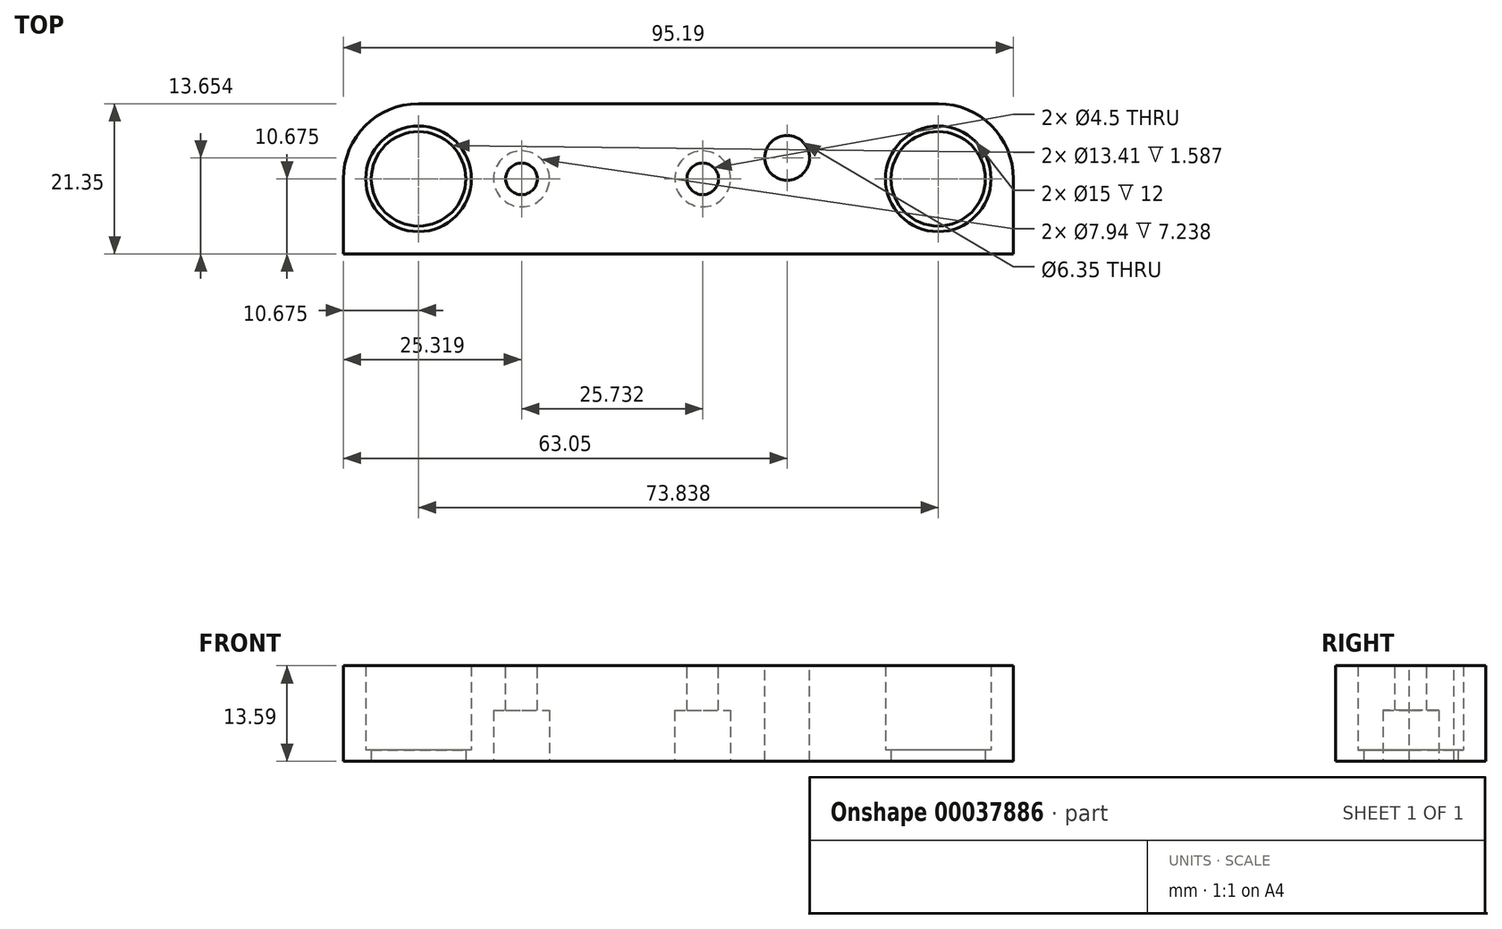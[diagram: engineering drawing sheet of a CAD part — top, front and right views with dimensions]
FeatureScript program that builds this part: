
annotation { "Feature Type Name" : "Feature", "Feature Type Description" : "" }
export const myFeature = defineFeature(function(context is Context, id is Id, definition is map)
    precondition{}
    {
        {
            var Q0;
            Q0=qCreatedBy(makeId("Top.planeOp"),FACE);
            var sketch = newSketch(context, id + "F0", { "sketchPlane" : qUnion([Q0])});
            skLineSegment(sketch, "E0.bottom", {"start": v(0, 0) * mm, "end": v(95.19, 0) * mm});
            skLineSegment(sketch, "E0.top", {"start": v(0, -21.35) * mm, "end": v(95.19, -21.35) * mm});
            skLineSegment(sketch, "E0.left", {"start": v(0, 0) * mm, "end": v(0, -21.35) * mm});
            skLineSegment(sketch, "E0.right", {"start": v(95.19, 0) * mm, "end": v(95.19, -21.35) * mm});
            skLineSegment(sketch, "E1", {"start": v(10.67, 0) * mm, "end": v(10.67, -10.67) * mm, "construction": true});
            skLineSegment(sketch, "E2", {"start": v(10.67, -10.67) * mm, "end": v(0, -10.67) * mm, "construction": true});
            skLineSegment(sketch, "E3", {"start": v(95.19, -10.67) * mm, "end": v(84.51, -10.67) * mm, "construction": true});
            skCircle(sketch, "E4", {"center": v(10.67, -10.67) * mm, "radius": 6.7 * mm});
            skCircle(sketch, "E5", {"center": v(84.51, -10.67) * mm, "radius": 6.7 * mm});
            skSolve(sketch);
        }
        {
            var Q0;
            Q0=qSketchRegion(id+"F0",true);
            extrude(context, id + "F1", {"entities" : qUnion([Q0]), "depth" : 1.59 * mm});
        }
        {
            var Q0;
            Q0=makeQuery(id+"F1.opExtrude","SWEPT_EDGE",EDGE,{"disambiguationData":[OSD([sQuery(id+"F0.wireOp",EDGE,"E0.bottom"),sQuery(id+"F0.wireOp",EDGE,"E0.left")])]});
            var Q1;
            Q1=makeQuery(id+"F1.opExtrude","SWEPT_EDGE",EDGE,{"disambiguationData":[OSD([sQuery(id+"F0.wireOp",EDGE,"E0.bottom"),sQuery(id+"F0.wireOp",EDGE,"E0.right")])]});
            fillet(context, id + "F2", {"entities" : qUnion([Q0, Q1]), "radius" : 10.67 * mm, "tangentPropagation" : true, "allowEdgeOverflow" : false});
        }
        {
            var Q0;
            Q0=makeQuery(id+"F1.opExtrude","CAP_FACE",FACE,{"disambiguationData":[OSD([sQuery(id+"F0.wireOp",EDGE,"E0.bottom"),sQuery(id+"F0.wireOp",EDGE,"E0.top"),sQuery(id+"F0.wireOp",EDGE,"E0.left"),sQuery(id+"F0.wireOp",EDGE,"E0.right"),sQuery(id+"F0.wireOp",EDGE,"E4"),sQuery(id+"F0.wireOp",EDGE,"E5")])],"isStart":false});
            var sketch = newSketch(context, id + "F3", { "sketchPlane" : qUnion([Q0])});
            skLineSegment(sketch, "E6.bottom", {"start": v(0, -10.67) * mm, "end": v(95.19, -10.67) * mm, "construction": true});
            skLineSegment(sketch, "E6.top", {"start": v(0, -15) * mm, "end": v(95.19, -15) * mm});
            skLineSegment(sketch, "E6.left", {"start": v(0, -10.67) * mm, "end": v(0, -15) * mm});
            skLineSegment(sketch, "E6.right", {"start": v(95.19, -10.67) * mm, "end": v(95.19, -15) * mm});
            skLineSegment(sketch, "E7", {"start": v(47.6, -15) * mm, "end": v(47.6, -21.35) * mm, "construction": true});
            skPoint(sketch, "E7.endSnap0", {"position": v(47.6, -21.35) * mm});
            skCircle(sketch, "E8", {"center": v(10.67, -10.67) * mm, "radius": 7.5 * mm});
            skCircle(sketch, "E9", {"center": v(84.51, -10.67) * mm, "radius": 7.5 * mm});
            skSolve(sketch);
        }
        {
            var Q0;
            {var subQ3=makeQuery(id+"F1.opExtrude","CAP_EDGE",EDGE,{"disambiguationData":[OSD([sQuery(id+"F0.wireOp",EDGE,"E0.top")])],"isStart":false});Q0=makeQuery(id+"F3.imprint","IMPRINT",FACE,{"disambiguationData":[TD([[makeQuery(id+"F3.imprint","IMPRINT",EDGE,{"derivedFrom":subQ3}),1.0]])]});}
            var Q1;
            {var subQ9=sQuery(id+"F3.wireOp",EDGE,"E6.left");Q1=makeQuery(id+"F3.imprint","IMPRINT",FACE,{"disambiguationData":[TD([[makeQuery(id+"F3.imprint","IMPRINT",EDGE,{"derivedFrom":subQ9}),1.0]])]});}
            extrude(context, id + "F4", {"entities" : qUnion([Q0, Q1]), "operationType" : NewBodyOperationType.ADD, "depth" : 12 * mm});
        }
        {
            var Q0;
            Q0=makeQuery(id+"F4.opExtrude","CAP_FACE",FACE,{"disambiguationData":[OSD([sQuery(id+"F0.wireOp",EDGE,"E0.bottom"),sQuery(id+"F0.wireOp",EDGE,"E0.top"),sQuery(id+"F0.wireOp",EDGE,"E0.left"),sQuery(id+"F0.wireOp",EDGE,"E0.right"),sQuery(id+"F0.wireOp",EDGE,"E4"),sQuery(id+"F0.wireOp",EDGE,"E5"),sQuery(id+"F3.wireOp",EDGE,"E6.top"),sQuery(id+"F3.wireOp",EDGE,"E6.left"),sQuery(id+"F3.wireOp",EDGE,"E6.right"),sQuery(id+"F3.wireOp",EDGE,"E8"),sQuery(id+"F3.wireOp",EDGE,"E9")])],"isStart":false});
            var sketch = newSketch(context, id + "F5", { "sketchPlane" : qUnion([Q0])});
            skLineSegment(sketch, "E10", {"start": v(47.6, -10.67) * mm, "end": v(51.05, -10.67) * mm, "construction": true});
            skPoint(sketch, "E11", {"position": v(47.6, -10.67) * mm});
            skCircle(sketch, "E12", {"center": v(51.05, -10.67) * mm, "radius": 2.25 * mm});
            skLineSegment(sketch, "E13", {"start": v(47.6, -10.67) * mm, "end": v(47.6, -21.35) * mm});
            skCircle(sketch, "E14", {"center": v(51.05, -10.67) * mm, "radius": 7.14 * mm, "construction": true});
            skCircle(sketch, "E15", {"center": v(63.05, -7.7) * mm, "radius": 5.22 * mm, "construction": true});
            skLineSegment(sketch, "E16", {"start": v(47.6, -10.67) * mm, "end": v(25.32, -10.67) * mm, "construction": true});
            skCircle(sketch, "E17", {"center": v(25.32, -10.67) * mm, "radius": 7.14 * mm, "construction": true});
            skCircle(sketch, "E18", {"center": v(63.05, -7.7) * mm, "radius": 3.18 * mm});
            skCircle(sketch, "E19", {"center": v(25.32, -10.67) * mm, "radius": 2.25 * mm});
            skLineSegment(sketch, "E20", {"start": v(84.51, -10.67) * mm, "end": v(84.51, -7.7) * mm, "construction": true});
            skLineSegment(sketch, "E21", {"start": v(84.51, -7.7) * mm, "end": v(63.05, -7.7) * mm, "construction": true});
            skSolve(sketch);
        }
        {
            var Q0;
            Q0=qSketchRegion(id+"F5",true);
            var Q1;
            Q1=makeQuery(id+"F1.opExtrude","CAP_FACE",FACE,{"disambiguationData":[OSD([sQuery(id+"F0.wireOp",EDGE,"E0.bottom"),sQuery(id+"F0.wireOp",EDGE,"E0.top"),sQuery(id+"F0.wireOp",EDGE,"E0.left"),sQuery(id+"F0.wireOp",EDGE,"E0.right"),sQuery(id+"F0.wireOp",EDGE,"E4"),sQuery(id+"F0.wireOp",EDGE,"E5")])],"isStart":true});
            extrude(context, id + "F6", {"entities" : qUnion([Q0]), "operationType" : NewBodyOperationType.REMOVE, "endBound" : BoundingType.UP_TO_SURFACE, "oppositeDirection" : true, "endBoundEntityFace" : qUnion([Q1]), "depth" : 25.4 * mm});
        }
        {
            var Q0;
            Q0=makeQuery(id+"F1.opExtrude","CAP_FACE",FACE,{"disambiguationData":[OSD([sQuery(id+"F0.wireOp",EDGE,"E0.bottom"),sQuery(id+"F0.wireOp",EDGE,"E0.top"),sQuery(id+"F0.wireOp",EDGE,"E0.left"),sQuery(id+"F0.wireOp",EDGE,"E0.right"),sQuery(id+"F0.wireOp",EDGE,"E4"),sQuery(id+"F0.wireOp",EDGE,"E5")])],"isStart":true});
            var sketch = newSketch(context, id + "F7", { "sketchPlane" : qUnion([Q0])});
            skCircle(sketch, "E22", {"center": v(51.05, 10.67) * mm, "radius": 3.97 * mm});
            skCircle(sketch, "E23", {"center": v(25.32, 10.67) * mm, "radius": 3.97 * mm});
            skSolve(sketch);
        }
        {
            var Q0;
            Q0=qSketchRegion(id+"F7",true);
            extrude(context, id + "F8", {"entities" : qUnion([Q0]), "operationType" : NewBodyOperationType.REMOVE, "oppositeDirection" : true, "depth" : 7.24 * mm});
        }
    });
